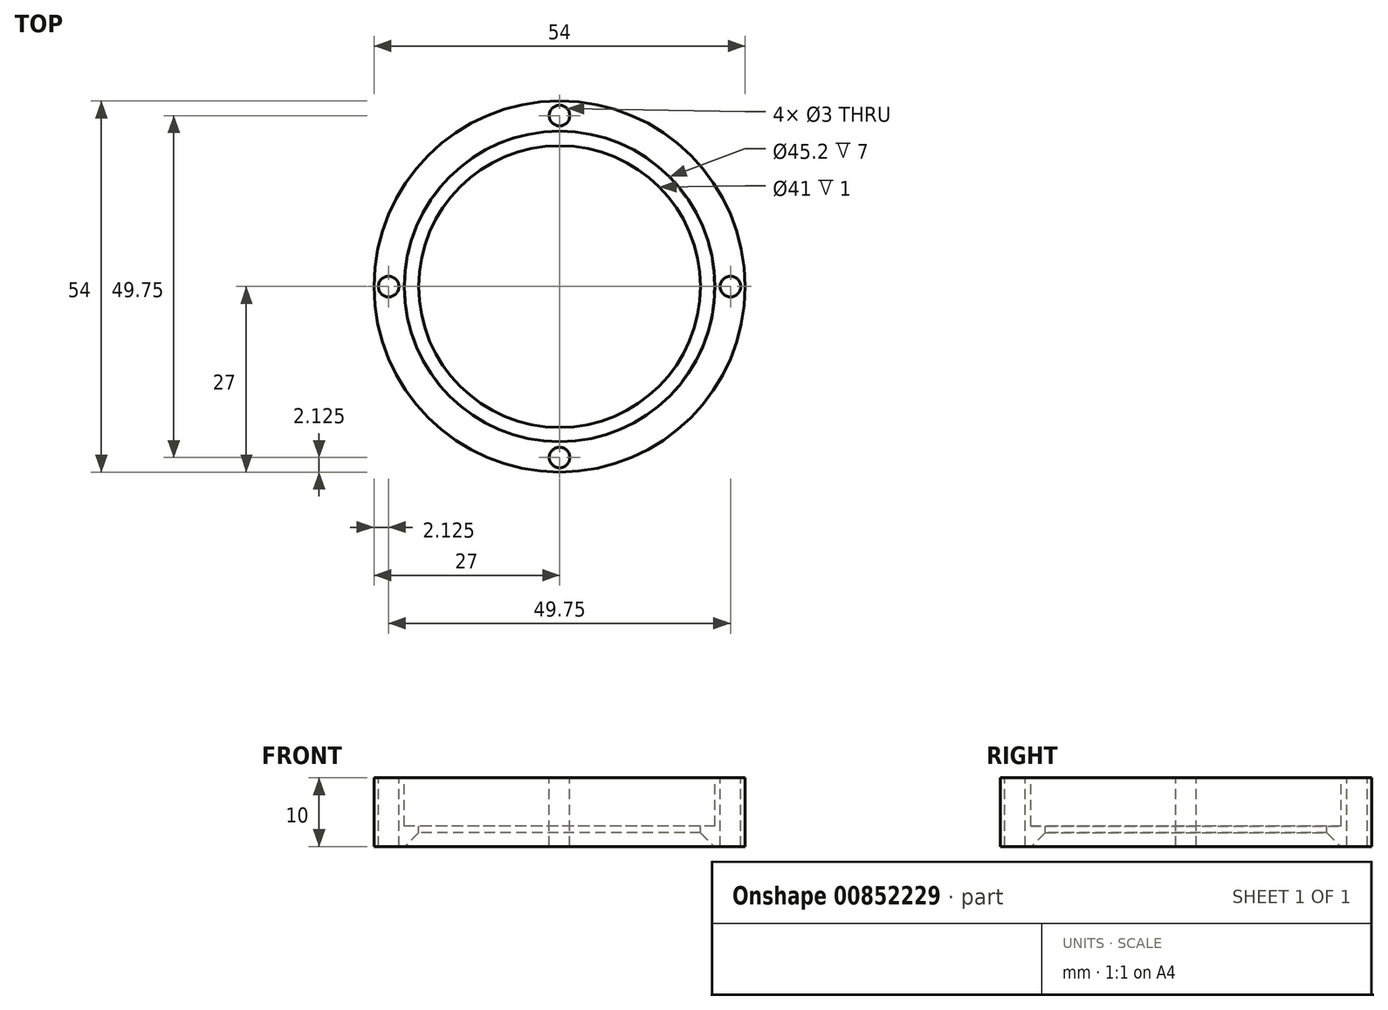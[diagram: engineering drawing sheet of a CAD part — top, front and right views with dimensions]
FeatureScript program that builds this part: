
annotation { "Feature Type Name" : "Feature", "Feature Type Description" : "" }
export const myFeature = defineFeature(function(context is Context, id is Id, definition is map)
    precondition{}
    {
        {
            var Q0;
            Q0=qCreatedBy(makeId("Top.planeOp"),FACE);
            var sketch = newSketch(context, id + "F0", { "sketchPlane" : qUnion([Q0])});
            skCircle(sketch, "E0", {"center": v(0, 0) * mm, "radius": 27 * mm});
            skSolve(sketch);
        }
        {
            var Q0;
            Q0=makeQuery(id+"F0.imprint","IMPRINT",FACE,{"disambiguationData":[TD([[makeQuery(id+"F0.imprint","IMPRINT",EDGE,{"derivedFrom":sQuery(id+"F0.wireOp",EDGE,"E0")}),1.0]])]});
            extrude(context, id + "F1", {"entities" : qUnion([Q0]), "depth" : 10 * mm, "offsetDistance" : 25 * mm});
        }
        {
            var Q0;
            Q0=makeQuery(id+"F1.opExtrude","CAP_FACE",FACE,{"disambiguationData":[OSD([sQuery(id+"F0.wireOp",EDGE,"E0")])],"isStart":false});
            var sketch = newSketch(context, id + "F2", { "sketchPlane" : qUnion([Q0])});
            skCircle(sketch, "E1", {"center": v(0, 0) * mm, "radius": 22.6 * mm});
            skSolve(sketch);
        }
        {
            var Q0;
            Q0=makeQuery(id+"F2.imprint","IMPRINT",FACE,{"disambiguationData":[TD([[makeQuery(id+"F2.imprint","IMPRINT",EDGE,{"derivedFrom":sQuery(id+"F2.wireOp",EDGE,"E1")}),1.0]])]});
            extrude(context, id + "F3", {"entities" : qUnion([Q0]), "operationType" : NewBodyOperationType.REMOVE, "oppositeDirection" : true, "depth" : 7 * mm, "offsetDistance" : 25 * mm});
        }
        {
            var Q0;
            Q0=makeQuery(id+"F3.boolean.opBoolean","COPY",FACE,{"derivedFrom":makeQuery(id+"F3.opExtrude","CAP_FACE",FACE,{"disambiguationData":[OSD([sQuery(id+"F2.wireOp",EDGE,"E1")])],"isStart":false})});
            var sketch = newSketch(context, id + "F4", { "sketchPlane" : qUnion([Q0])});
            skCircle(sketch, "E2", {"center": v(0, 0) * mm, "radius": 20.5 * mm});
            skSolve(sketch);
        }
        {
            var Q0;
            Q0=makeQuery(id+"F4.imprint","IMPRINT",FACE,{"disambiguationData":[TD([[makeQuery(id+"F4.imprint","IMPRINT",EDGE,{"derivedFrom":sQuery(id+"F4.wireOp",EDGE,"E2")}),1.0]])]});
            extrude(context, id + "F5", {"entities" : qUnion([Q0]), "operationType" : NewBodyOperationType.REMOVE, "endBound" : BoundingType.THROUGH_ALL, "oppositeDirection" : true, "depth" : 25 * mm, "offsetDistance" : 25 * mm});
        }
        {
            var Q0;
            Q0=makeQuery(id+"F1.opExtrude","CAP_FACE",FACE,{"disambiguationData":[OSD([sQuery(id+"F0.wireOp",EDGE,"E0")])],"isStart":false});
            var sketch = newSketch(context, id + "F6", { "sketchPlane" : qUnion([Q0])});
            skCircle(sketch, "E3", {"center": v(0, 0) * mm, "radius": 24.88 * mm, "construction": true});
            skCircle(sketch, "E4", {"center": v(-24.88, 0) * mm, "radius": 1.5 * mm});
            skCircle(sketch, "E5.MirrorC", {"center": v(24.88, 0) * mm, "radius": 1.5 * mm});
            skCircle(sketch, "E6", {"center": v(0, 24.88) * mm, "radius": 1.5 * mm});
            skCircle(sketch, "E7.MirrorC", {"center": v(0, -24.88) * mm, "radius": 1.5 * mm});
            skSolve(sketch);
        }
        {
            var Q0;
            Q0 = qSketchRegion(id + "F6", true);
            extrude(context, id + "F7", {"entities" : qUnion([Q0]), "operationType" : NewBodyOperationType.REMOVE, "endBound" : BoundingType.THROUGH_ALL, "oppositeDirection" : true, "depth" : 25 * mm, "offsetDistance" : 25 * mm});
        }
        {
            var Q0;
            Q0=makeQuery(id+"F5.boolean.opBoolean","INTERSECT",EDGE,{"derivedFrom":[makeQuery(id+"F1.opExtrude","CAP_FACE",FACE,{"disambiguationData":[OSD([sQuery(id+"F0.wireOp",EDGE,"E0")])],"isStart":true}),makeQuery(id+"F5.opExtrude","SWEPT_FACE",FACE,{"disambiguationData":[OSD([sQuery(id+"F4.wireOp",EDGE,"E2")])]})]});
            chamfer(context, id + "F8", {"entities" : qUnion([Q0]), "width" : 2 * mm, "tangentPropagation" : true});
        }
    });
